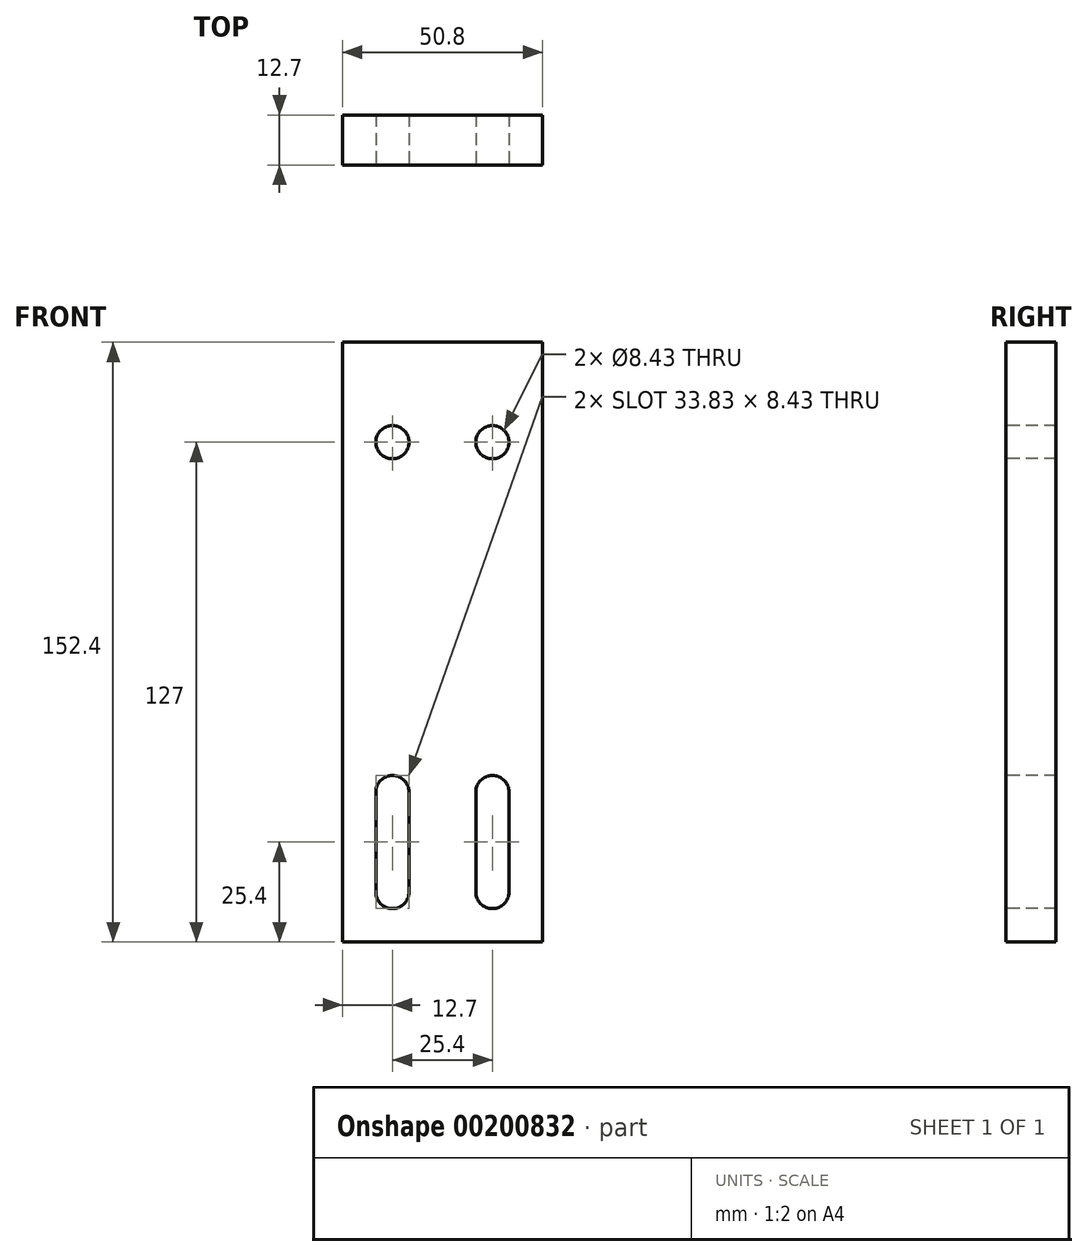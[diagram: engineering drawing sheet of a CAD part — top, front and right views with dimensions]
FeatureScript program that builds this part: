
annotation { "Feature Type Name" : "Feature", "Feature Type Description" : "" }
export const myFeature = defineFeature(function(context is Context, id is Id, definition is map)
    precondition{}
    {
        {
            var Q0;
            Q0=qCreatedBy(makeId("Front.planeOp"),FACE);
            var sketch = newSketch(context, id + "F0", { "sketchPlane" : qUnion([Q0])});
            skLineSegment(sketch, "E0.bottom", {"start": v(0, 0) * mm, "end": v(50.8, 0) * mm});
            skLineSegment(sketch, "E0.top", {"start": v(0, 152.4) * mm, "end": v(50.8, 152.4) * mm});
            skLineSegment(sketch, "E0.left", {"start": v(0, 0) * mm, "end": v(0, 152.4) * mm});
            skLineSegment(sketch, "E0.right", {"start": v(50.8, 0) * mm, "end": v(50.8, 152.4) * mm});
            skSolve(sketch);
        }
        {
            var Q0;
            Q0 = qSketchRegion(id + "F0", true);
            extrude(context, id + "F1", {"entities" : qUnion([Q0]), "depth" : 12.7 * mm});
        }
        {
            var Q0;
            Q0=makeQuery(id+"F1.opExtrude","CAP_FACE",FACE,{"disambiguationData":[OSD([sQuery(id+"F0.wireOp",EDGE,"E0.bottom"),sQuery(id+"F0.wireOp",EDGE,"E0.top"),sQuery(id+"F0.wireOp",EDGE,"E0.left"),sQuery(id+"F0.wireOp",EDGE,"E0.right")])],"isStart":false});
            var sketch = newSketch(context, id + "F2", { "sketchPlane" : qUnion([Q0])});
            skPoint(sketch, "E1", {"position": v(12.7, 127) * mm});
            skPoint(sketch, "E2", {"position": v(38.1, 127) * mm});
            skSolve(sketch);
        }
        {
            var Q0;
            Q0=makeQuery(id+"F2.imprint","IMPRINT",FACE,{"disambiguationData":[TD([[makeQuery(id+"F2.imprint","IMPRINT",EDGE,{"derivedFrom":makeQuery(id+"F1.opExtrude","CAP_EDGE",EDGE,{"disambiguationData":[OSD([sQuery(id+"F0.wireOp",EDGE,"E0.bottom")])],"isStart":false})}),1.0]])]});
            var sketch = newSketch(context, id + "F3", { "sketchPlane" : qUnion([Q0])});
            skPoint(sketch, "E3", {"position": v(12.7, 38.1) * mm});
            skPoint(sketch, "E4", {"position": v(12.7, 12.7) * mm});
            skPoint(sketch, "E5", {"position": v(38.1, 12.7) * mm});
            skPoint(sketch, "E6", {"position": v(38.1, 38.1) * mm});
            skSolve(sketch);
        }
        {
            var Q0;
            Q0=sQuery(id+"F2.wireOp",VERTEX,"E1");
            var Q1;
            Q1=sQuery(id+"F2.wireOp",VERTEX,"E2");
            var Q2;
            Q2=makeQuery(id+"F1.opExtrude","SWEPT_BODY",BODY,{"disambiguationData":[OSD([sQuery(id+"F0.wireOp",EDGE,"E0.bottom"),sQuery(id+"F0.wireOp",EDGE,"E0.top"),sQuery(id+"F0.wireOp",EDGE,"E0.left"),sQuery(id+"F0.wireOp",EDGE,"E0.right")])]});
            hole(context, id + "F4", {"style" : HoleStyle.SIMPLE, "endStyle" : HoleEndStyle.THROUGH, "standardTappedOrClearance" : lookupTablePath({ "standard" : "ANSI", "fit" : "Normal (ASME)", "size" : "5/16", "type" : "Clearance" }), "standardBlindInLast" : lookupTablePath({ "fit" : "Free", "standard" : "ANSI", "size" : "5/16", "type" : "Clearance" }), "holeDiameter" : 8.43 * mm, "locations" : qUnion([Q0, Q1]), "scope" : qUnion([Q2]), "isTappedThrough" : true});
        }
        {
            var Q0;
            Q0=makeQuery(id+"F3.imprint","IMPRINT",FACE,{"disambiguationData":[TD([[makeQuery(id+"F3.imprint","IMPRINT",EDGE,{"derivedFrom":makeQuery(id+"F2.imprint","IMPRINT",EDGE,{"derivedFrom":makeQuery(id+"F1.opExtrude","CAP_EDGE",EDGE,{"disambiguationData":[OSD([sQuery(id+"F0.wireOp",EDGE,"E0.bottom")])],"isStart":false})})}),1.0]])]});
            var sketch = newSketch(context, id + "F5", { "sketchPlane" : qUnion([Q0])});
            skArc(sketch, "E7", {"start": v(16.92, 38.1) * mm, "mid": v(12.7, 42.32) * mm, "end": v(8.48, 38.1) * mm});
            skArc(sketch, "E8", {"start": v(8.48, 12.7) * mm, "mid": v(12.7, 8.48) * mm, "end": v(16.92, 12.7) * mm});
            skArc(sketch, "E9", {"start": v(42.32, 38.1) * mm, "mid": v(38.1, 42.32) * mm, "end": v(33.88, 38.1) * mm});
            skArc(sketch, "E10", {"start": v(33.88, 12.7) * mm, "mid": v(38.1, 8.48) * mm, "end": v(42.32, 12.7) * mm});
            skLineSegment(sketch, "E11", {"start": v(8.48, 38.1) * mm, "end": v(8.48, 12.7) * mm});
            skLineSegment(sketch, "E12", {"start": v(16.92, 12.7) * mm, "end": v(16.92, 38.1) * mm});
            skLineSegment(sketch, "E13", {"start": v(33.88, 38.1) * mm, "end": v(33.88, 12.7) * mm});
            skLineSegment(sketch, "E14", {"start": v(42.32, 38.1) * mm, "end": v(42.32, 12.7) * mm});
            skSolve(sketch);
        }
        {
            var Q0;
            Q0 = qSketchRegion(id + "F5", true);
            extrude(context, id + "F6", {"entities" : qUnion([Q0]), "operationType" : NewBodyOperationType.REMOVE, "endBound" : BoundingType.THROUGH_ALL, "oppositeDirection" : true, "depth" : 25.4 * mm});
        }
    });
